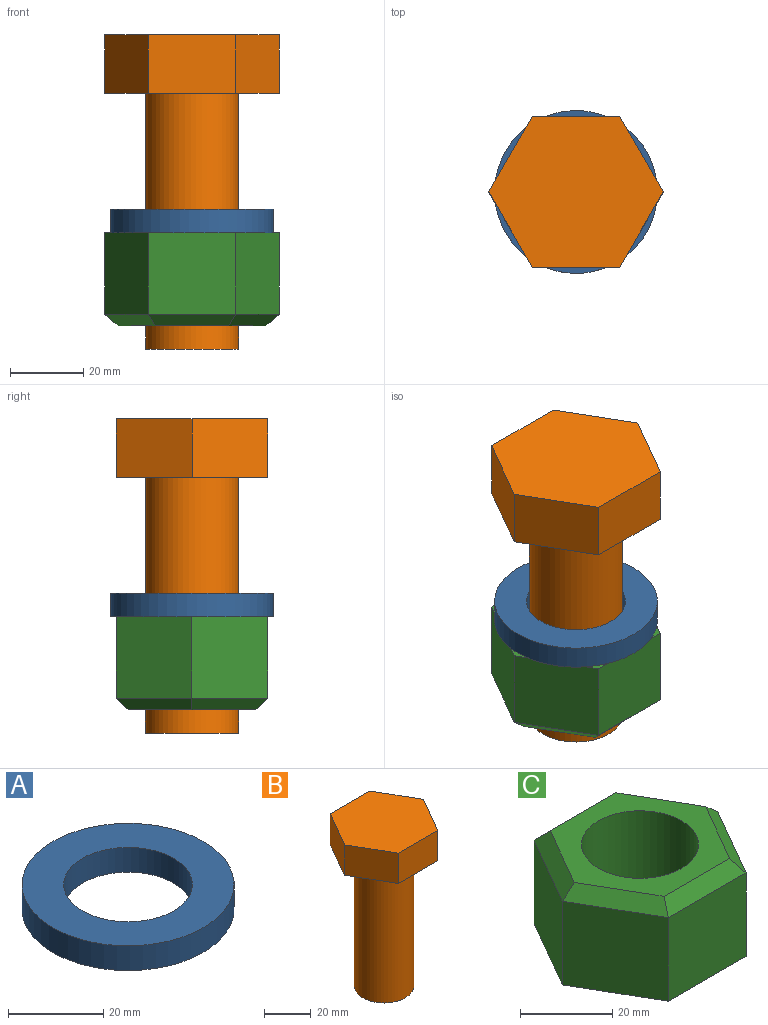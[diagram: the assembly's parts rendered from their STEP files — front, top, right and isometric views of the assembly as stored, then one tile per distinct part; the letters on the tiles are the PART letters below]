
ASSEMBLY  parts=3 mates=2
PART A: 4 faces, bbox 44.5x44.5x6.4 mm
  f0: cylinder r=13.49mm len=26.99mm, axis (0,0,-1), area 538.4mm2, adj f2,f3
  f1: cylinder r=22.23mm len=44.45mm, axis (0,0,-1), area 886.7mm2, adj f2,f3
  f2: plane 44.45x44.45mm, normal (0,0,1), area 979.8mm2, adj f0,f1
  f3: plane 44.45x44.45mm, normal (0,0,-1), area 979.8mm2, adj f0,f1
PART B: 10 faces, bbox 47.7x41.3x85.7 mm
  f0: cylinder r=12.7mm len=69.85mm, axis (0,0,1), area 5573.8mm2, adj f1,f9
  f1: plane 25.4x25.4mm, normal (0,0,-1), area 506.7mm2, adj f0
  f2: plane 20.64x15.88mm, normal (-0.87,0.5,0), area 378.3mm2, adj f3,f7,f8,f9
  f3: plane 20.64x15.88mm, normal (-0.87,-0.5,0), area 378.3mm2, adj f2,f4,f8,f9
  f4: plane 23.83x15.88mm, normal (0,-1,0), area 378.3mm2, adj f3,f5,f8,f9
  f5: plane 20.64x15.88mm, normal (0.87,-0.5,0), area 378.3mm2, adj f4,f6,f8,f9
  f6: plane 20.64x15.88mm, normal (0.87,0.5,0), area 378.3mm2, adj f5,f7,f8,f9
  f7: plane 23.83x15.88mm, normal (0,1,0), area 378.3mm2, adj f2,f6,f8,f9
  f8: plane 47.66x41.28mm, normal (0,0,1), area 1475.4mm2, adj f2,f3,f4,f5,f6,f7
  f9: plane 47.66x41.28mm, normal (0,0,-1), area 968.7mm2, adj f0,f2,f3,f4,f5,f6,f7
PART C: 15 faces, bbox 47.7x41.3x25.4 mm
  f0: plane 22.23x20.64mm, normal (-0.87,0.5,0), area 529.6mm2, adj f1,f6,f8,f9
  f1: plane 22.23x20.64mm, normal (-0.87,-0.5,0), area 529.6mm2, adj f0,f2,f8,f11
  f2: plane 23.83x22.23mm, normal (0,-1,0), area 529.6mm2, adj f1,f3,f8,f13
  f3: plane 22.23x20.64mm, normal (0.87,-0.5,0), area 529.6mm2, adj f2,f4,f8,f14
  f4: plane 22.23x20.64mm, normal (0.87,0.5,0), area 529.6mm2, adj f3,f6,f8,f12
  f5: cylinder r=12.7mm len=25.4mm, axis (0,0,-1), area 2026.8mm2, adj f7,f8
  f6: plane 23.83x22.23mm, normal (0,1,0), area 529.6mm2, adj f0,f4,f8,f10
  f7: plane 40.33x34.93mm, normal (0,0,1), area 549.6mm2, adj f5,f9,f10,f11,f12,f13,f14
  f8: plane 47.66x41.28mm, normal (0,0,-1), area 968.7mm2, adj f0,f1,f2,f3,f4,f5,f6
  f9: plane 20.64x13.75mm, normal (-0.61,0.35,0.71), area 98.8mm2, adj f0,f7,f10,f11
  f10: plane 23.83x3.18mm, normal (0,0.71,0.71), area 98.8mm2, adj f6,f7,f9,f12
  f11: plane 20.64x13.75mm, normal (-0.61,-0.35,0.71), area 98.8mm2, adj f1,f7,f9,f13
  f12: plane 20.64x13.75mm, normal (0.61,0.35,0.71), area 98.8mm2, adj f4,f7,f10,f14
  f13: plane 23.83x3.18mm, normal (0,-0.71,0.71), area 98.8mm2, adj f2,f7,f11,f14
  f14: plane 20.64x13.75mm, normal (0.61,-0.35,0.71), area 98.8mm2, adj f3,f7,f12,f13
PLACE A t=(19.44,3.99,-14.02)mm
PLACE B t=(19.44,3.99,24.08)mm
PLACE C rot(axis=(1,0,0),180deg) t=(19.44,3.99,-14.02)mm
MATE fastened C.f5 <-> A.f0  axis (0,0,1) through (19.44,3.99,-14.02)mm
MATE fastened C.f5 <-> B.f0  axis (0,0,1) through (19.44,3.99,-39.42)mm
